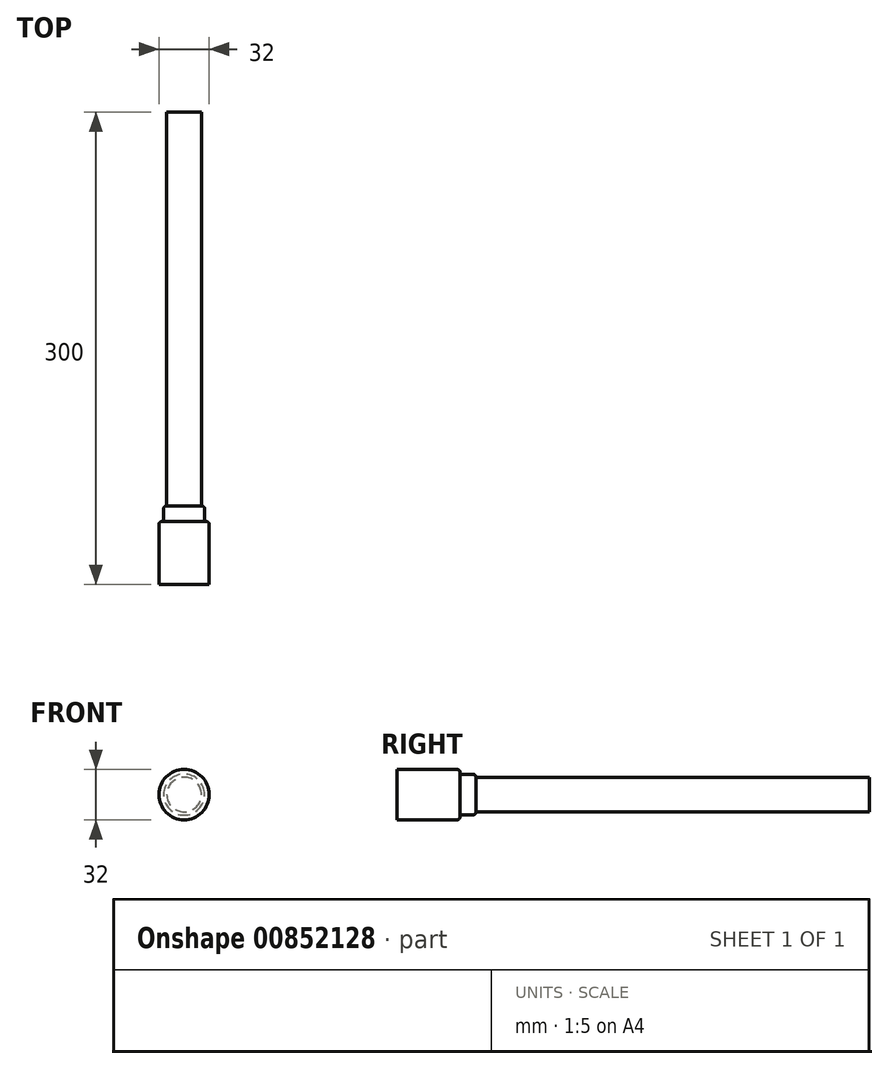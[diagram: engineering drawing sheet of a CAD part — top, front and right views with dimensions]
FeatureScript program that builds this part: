
annotation { "Feature Type Name" : "Feature", "Feature Type Description" : "" }
export const myFeature = defineFeature(function(context is Context, id is Id, definition is map)
    precondition{}
    {
        {
            var Q0;
            Q0=qCreatedBy(makeId("Front.planeOp"),FACE);
            var sketch = newSketch(context, id + "F0", { "sketchPlane" : qUnion([Q0])});
            skCircle(sketch, "E0", {"center": v(0, 0) * mm, "radius": 11 * mm});
            skSolve(sketch);
        }
        {
            var Q0;
            Q0=makeQuery(id+"F0.imprint","IMPRINT",FACE,{"disambiguationData":[TD([[makeQuery(id+"F0.imprint","IMPRINT",EDGE,{"derivedFrom":sQuery(id+"F0.wireOp",EDGE,"E0")}),1.0]])]});
            extrude(context, id + "F1", {"entities" : qUnion([Q0]), "depth" : 250 * mm, "offsetDistance" : 25 * mm});
        }
        {
            var Q0;
            Q0=makeQuery(id+"F1.opExtrude","CAP_FACE",FACE,{"disambiguationData":[OSD([sQuery(id+"F0.wireOp",EDGE,"E0")])],"isStart":false});
            var sketch = newSketch(context, id + "F2", { "sketchPlane" : qUnion([Q0])});
            skCircle(sketch, "E1", {"center": v(0, 0) * mm, "radius": 13 * mm});
            skSolve(sketch);
        }
        {
            var Q0;
            Q0=makeQuery(id+"F2.imprint","IMPRINT",FACE,{"disambiguationData":[TD([[makeQuery(id+"F2.imprint","IMPRINT",EDGE,{"derivedFrom":sQuery(id+"F2.wireOp",EDGE,"E1")}),1.0]])]});
            var Q1;
            Q1=makeQuery(id+"F2.imprint","IMPRINT",FACE,{"disambiguationData":[TD([[makeQuery(id+"F2.imprint","IMPRINT",EDGE,{"derivedFrom":makeQuery(id+"F1.opExtrude","CAP_EDGE",EDGE,{"disambiguationData":[OSD([sQuery(id+"F0.wireOp",EDGE,"E0")])],"isStart":false})}),1.0]])]});
            extrude(context, id + "F3", {"entities" : qUnion([Q0, Q1]), "operationType" : NewBodyOperationType.ADD, "depth" : 10 * mm, "offsetDistance" : 25 * mm});
        }
        {
            var Q0;
            Q0=makeQuery(id+"F3.opExtrude","CAP_EDGE",EDGE,{"disambiguationData":[OSD([sQuery(id+"F2.wireOp",EDGE,"E1")])],"isStart":true});
            fillet(context, id + "F4", {"entities" : qUnion([Q0]), "radius" : 2 * mm, "tangentPropagation" : true, "allowEdgeOverflow" : false});
        }
        {
            var Q0;
            Q0=makeQuery(id+"F3.opExtrude","CAP_FACE",FACE,{"disambiguationData":[OSD([sQuery(id+"F2.wireOp",EDGE,"E1")])],"isStart":false});
            var sketch = newSketch(context, id + "F5", { "sketchPlane" : qUnion([Q0])});
            skCircle(sketch, "E2", {"center": v(0, 0) * mm, "radius": 16 * mm});
            skSolve(sketch);
        }
        {
            var Q0;
            Q0=makeQuery(id+"F5.imprint","IMPRINT",FACE,{"disambiguationData":[TD([[makeQuery(id+"F5.imprint","IMPRINT",EDGE,{"derivedFrom":sQuery(id+"F5.wireOp",EDGE,"E2")}),1.0]])]});
            var Q1;
            Q1=makeQuery(id+"F5.imprint","IMPRINT",FACE,{"disambiguationData":[TD([[makeQuery(id+"F5.imprint","IMPRINT",EDGE,{"derivedFrom":makeQuery(id+"F3.opExtrude","CAP_EDGE",EDGE,{"disambiguationData":[OSD([sQuery(id+"F2.wireOp",EDGE,"E1")])],"isStart":false})}),1.0]])]});
            extrude(context, id + "F6", {"entities" : qUnion([Q0, Q1]), "operationType" : NewBodyOperationType.ADD, "depth" : 40 * mm, "offsetDistance" : 25 * mm});
        }
        {
            var Q0;
            Q0=makeQuery(id+"F6.opExtrude","CAP_EDGE",EDGE,{"disambiguationData":[OSD([sQuery(id+"F5.wireOp",EDGE,"E2")])],"isStart":true});
            fillet(context, id + "F7", {"entities" : qUnion([Q0]), "radius" : 2 * mm, "tangentPropagation" : true, "allowEdgeOverflow" : false});
        }
    });
